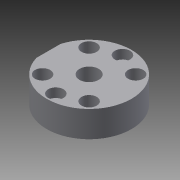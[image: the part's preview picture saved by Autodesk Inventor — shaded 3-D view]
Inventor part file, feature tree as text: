
AUTODESK INVENTOR PART (.ipt)
format: ipt  version: 2014 SP2 (Build 180246200, 246)  size: 264,704 bytes
history: native  units: in
note: dims shown in document units (in); Inventor stores cm internally (conversion verified against a paired STEP export)
features: other x308, sketch x8, hole x4, revolve x3, extrude x1, thread x1, pattern_linear x1
ambient origin geometry x8: Origin, YZ Plane, XZ Plane, XY Plane, X Axis, Y Axis, Z Axis, Center Point
bodies: Solid1 (feature_tree)
feature tree (326):
  revolve  "Revolution1"  [1 undecoded]
  extrude  "Extrusion1"  Depth=0.1831in TaperAngle=0.0deg
  revolve  "Revolution2"  Angle=360.0deg
  thread  "Thread1"  [1 undecoded]
  hole  "Hole1"  [1 undecoded]
  revolve  "Revolution3"  [1 undecoded]
  hole  "Hole2"  [1 undecoded]
  hole  "Hole3"  [1 undecoded]
  hole  "Hole4"  [1 undecoded]
  pattern_linear  "Rectangular Pattern1"  [2 undecoded]
  other  "a1_XY"
  other  "a1_YZ"
  other  "a1_ZX"
  other  "a1_X"
  other  "a1_Y"
  other  "a1_Z"
  other  "a1_Center"
  other  "a2_XY"
  other  "a2_YZ"
  other  "a2_ZX"
  other  "a2_X"
  other  "a2_Y"
  other  "a2_Z"
  other  "a2_Center"
  other  "ab_tr1_XY"
  other  "ab_tr1_YZ"
  other  "ab_tr1_ZX"
  other  "ab_tr1_X"
  other  "ab_tr1_Y"
  other  "ab_tr1_Z"
  other  "ab_tr1_Center"
  other  "ab_tr2_XY"
  other  "ab_tr2_YZ"
  other  "ab_tr2_ZX"
  other  "ab_tr2_X"
  other  "ab_tr2_Y"
  other  "ab_tr2_Z"
  other  "ab_tr2_Center"
  other  "ab_tr3_XY"
  other  "ab_tr3_YZ"
  other  "ab_tr3_ZX"
  other  "ab_tr3_X"
  other  "ab_tr3_Y"
  other  "ab_tr3_Z"
  other  "ab_tr3_Center"
  other  "ab_tr4_XY"
  other  "ab_tr4_YZ"
  other  "ab_tr4_ZX"
  other  "ab_tr4_X"
  other  "ab_tr4_Y"
  other  "ab_tr4_Z"
  other  "ab_tr4_Center"
  other  "ar3_XY"
  other  "ar3_YZ"
  other  "ar3_ZX"
  other  "ar3_X"
  other  "ar3_Y"
  other  "ar3_Z"
  other  "ar3_Center"
  other  "ar4_XY"
  other  "ar4_YZ"
  other  "ar4_ZX"
  other  "ar4_X"
  other  "ar4_Y"
  other  "ar4_Z"
  other  "ar4_Center"
  other  "ar5_XY"
  other  "ar5_YZ"
  other  "ar5_ZX"
  other  "ar5_X"
  other  "ar5_Y"
  other  "ar5_Z"
  other  "ar5_Center"
  other  "ar6_XY"
  other  "ar6_YZ"
  other  "ar6_ZX"
  other  "ar6_X"
  other  "ar6_Y"
  other  "ar6_Z"
  other  "ar6_Center"
  other  "b1_XY"
  other  "b1_YZ"
  other  "b1_ZX"
  other  "b1_X"
  other  "b1_Y"
  other  "b1_Z"
  other  "b1_Center"
  other  "j_XY"
  other  "j_YZ"
  other  "j_ZX"
  other  "j_X"
  other  "j_Y"
  other  "j_Z"
  other  "j_Center"
  other  "k1_XY"
  other  "k1_YZ"
  other  "k1_ZX"
  other  "k1_X"
  other  "k1_Y"
  other  "k1_Z"
  other  "k1_Center"
  other  "k2_XY"
  other  "k2_YZ"
  other  "k2_ZX"
  other  "k2_X"
  other  "k2_Y"
  other  "k2_Z"
  other  "k2_Center"
  other  "l1_XY"
  other  "l1_YZ"
  other  "l1_ZX"
  other  "l1_X"
  other  "l1_Y"
  other  "l1_Z"
  other  "l1_Center"
  other  "l2_XY"
  other  "l2_YZ"
  other  "l2_ZX"
  other  "l2_X"
  other  "l2_Y"
  other  "l2_Z"
  other  "l2_Center"
  other  "nut_XY"
  other  "nut_YZ"
  other  "nut_ZX"
  other  "nut_X"
  other  "nut_Y"
  other  "nut_Z"
  other  "nut_Center"
  other  "po1_XY"
  other  "po1_YZ"
  other  "po1_ZX"
  other  "po1_X"
  other  "po1_Y"
  other  "po1_Z"
  other  "po1_Center"
  other  "po2_XY"
  other  "po2_YZ"
  other  "po2_ZX"
  other  "po2_X"
  other  "po2_Y"
  other  "po2_Z"
  other  "po2_Center"
  other  "po3_XY"
  other  "po3_YZ"
  other  "po3_ZX"
  other  "po3_X"
  other  "po3_Y"
  other  "po3_Z"
  other  "po3_Center"
  other  "po4_XY"
  other  "po4_YZ"
  other  "po4_ZX"
  other  "po4_X"
  other  "po4_Y"
  other  "po4_Z"
  other  "po4_Center"
  other  "r7_XY"
  other  "r7_YZ"
  other  "r7_ZX"
  other  "r7_X"
  other  "r7_Y"
  other  "r7_Z"
  other  "r7_Center"
  other  "r71_XY"
  other  "r71_YZ"
  other  "r71_ZX"
  other  "r71_X"
  other  "r71_Y"
  other  "r71_Z"
  other  "r71_Center"
  other  "r72_XY"
  other  "r72_YZ"
  other  "r72_ZX"
  other  "r72_X"
  other  "r72_Y"
  other  "r72_Z"
  other  "r72_Center"
  other  "r73_XY"
  other  "r73_YZ"
  other  "r73_ZX"
  other  "r73_X"
  other  "r73_Y"
  other  "r73_Z"
  other  "r73_Center"
  other  "rg_XY"
  other  "rg_YZ"
  other  "rg_ZX"
  other  "rg_X"
  other  "rg_Y"
  other  "rg_Z"
  other  "rg_Center"
  other  "rh_XY"
  other  "rh_YZ"
  other  "rh_ZX"
  other  "rh_X"
  other  "rh_Y"
  other  "rh_Z"
  other  "rh_Center"
  other  "rs_1_XY"
  other  "rs_1_YZ"
  other  "rs_1_ZX"
  other  "rs_1_X"
  other  "rs_1_Y"
  other  "rs_1_Z"
  other  "rs_1_Center"
  other  "rs_2_XY"
  other  "rs_2_YZ"
  other  "rs_2_ZX"
  other  "rs_2_X"
  other  "rs_2_Y"
  other  "rs_2_Z"
  other  "rs_2_Center"
  other  "rs_3_XY"
  other  "rs_3_YZ"
  other  "rs_3_ZX"
  other  "rs_3_X"
  other  "rs_3_Y"
  other  "rs_3_Z"
  other  "rs_3_Center"
  other  "rs_4_XY"
  other  "rs_4_YZ"
  other  "rs_4_ZX"
  other  "rs_4_X"
  other  "rs_4_Y"
  other  "rs_4_Z"
  other  "rs_4_Center"
  other  "sc1_XY"
  other  "sc1_YZ"
  other  "sc1_ZX"
  other  "sc1_X"
  other  "sc1_Y"
  other  "sc1_Z"
  other  "sc1_Center"
  other  "sc2_XY"
  other  "sc2_YZ"
  other  "sc2_ZX"
  other  "sc2_X"
  other  "sc2_Y"
  other  "sc2_Z"
  other  "sc2_Center"
  other  "sc3_XY"
  other  "sc3_YZ"
  other  "sc3_ZX"
  other  "sc3_X"
  other  "sc3_Y"
  other  "sc3_Z"
  other  "sc3_Center"
  other  "sc4_XY"
  other  "sc4_YZ"
  other  "sc4_ZX"
  other  "sc4_X"
  other  "sc4_Y"
  other  "sc4_Z"
  other  "sc4_Center"
  other  "to_dummy_XY"
  other  "to_dummy_YZ"
  other  "to_dummy_ZX"
  other  "to_dummy_X"
  other  "to_dummy_Y"
  other  "to_dummy_Z"
  other  "to_dummy_Center"
  other  "to_nut_XY"
  other  "to_nut_YZ"
  other  "to_nut_ZX"
  other  "to_nut_X"
  other  "to_nut_Y"
  other  "to_nut_Z"
  other  "to_nut_Center"
  other  "to_rod_XY"
  other  "to_rod_YZ"
  other  "to_rod_ZX"
  other  "to_rod_X"
  other  "to_rod_Y"
  other  "to_rod_Z"
  other  "to_rod_Center"
  other  "to_tube_XY"
  other  "to_tube_YZ"
  other  "to_tube_ZX"
  other  "to_tube_X"
  other  "to_tube_Y"
  other  "to_tube_Z"
  other  "to_tube_Center"
  other  "to_wiper_XY"
  other  "to_wiper_YZ"
  other  "to_wiper_ZX"
  other  "to_wiper_X"
  other  "to_wiper_Y"
  other  "to_wiper_Z"
  other  "to_wiper_Center"
  other  "track1_XY"
  other  "track1_YZ"
  other  "track1_ZX"
  other  "track1_X"
  other  "track1_Y"
  other  "track1_Z"
  other  "track1_Center"
  other  "track2_XY"
  other  "track2_YZ"
  other  "track2_ZX"
  other  "track2_X"
  other  "track2_Y"
  other  "track2_Z"
  other  "track2_Center"
  other  "track3_XY"
  other  "track3_YZ"
  other  "track3_ZX"
  other  "track3_X"
  other  "track3_Y"
  other  "track3_Z"
  other  "track3_Center"
  other  "track4_XY"
  other  "track4_YZ"
  other  "track4_ZX"
  other  "track4_X"
  other  "track4_Y"
  other  "track4_Z"
  other  "track4_Center"
  sketch  "Sketch_1"  dims[d0=360.0deg d1=0.344in d2=0.0in]
  sketch  "Sketch_63"
  sketch  "Sketch_37"  dims[d41=0.0in d42=0.0in d43=0.0in d44=0.0in d45=0.0in d46=0.0in d47=0.0in d48=0.0in d49=0.0in d50=0.0in d51=0.0in d52=0.0in d53=0.0in d54=0.0in d55=0.0in d56=0.0in d57=0.0in d58=0.0in d59=0.0in d60=0.0in d61=0.0in d62=0.0in d63=0.0in d64=0.0in d65=0.0in d66=0.0in d67=0.0in d68=0.0in d69=0.0in d70=0.0in]
  sketch  "Sketch4"  dims[d3=360.0deg d4=0.1831in d5=0.0in]
  sketch  "Sketch_9"  dims[d28=0.1285in d29=0.75in d30=0.2in d31=0.15in d32=0.5635in d33=0.344in d34=0.0in d35=0.7874in d37=0.6109in d38=0.7874in d40=0.6109in]
  sketch  "Sketch6"  dims[d6=0.252in d7=0.75in d8=0.375in d9=0.25in d10=0.5635in d11=0.344in d12=0.0in d13=360.0deg]
  sketch  "Sketch7"  dims[d14=0.1285in d15=0.75in d16=0.2in d17=0.12in d18=0.5635in d19=0.344in d20=0.0in]
  sketch  "Sketch8"  dims[d21=0.1285in d22=0.75in d23=0.2in d24=0.12in d25=0.5635in d26=0.344in d27=0.0in]
note: 9 required parameter values undecoded (feature->parameter linkage not recoverable at this tier; creation-order binding heuristic only, values carry confidence <= 0.55)